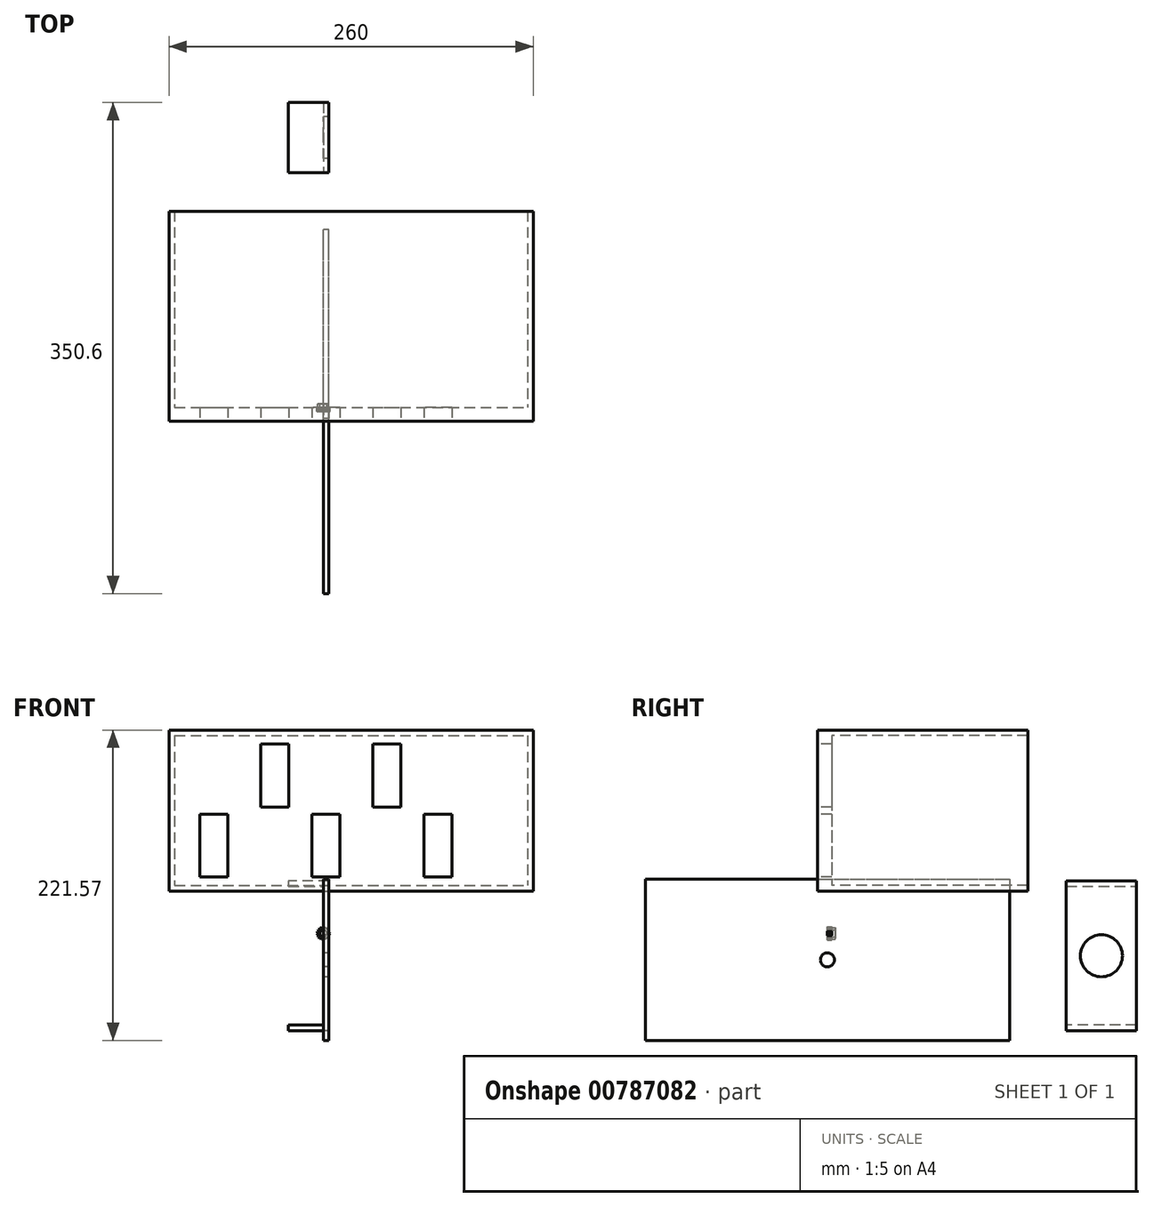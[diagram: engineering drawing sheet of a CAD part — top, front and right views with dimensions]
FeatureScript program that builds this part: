
annotation { "Feature Type Name" : "Feature", "Feature Type Description" : "" }
export const myFeature = defineFeature(function(context is Context, id is Id, definition is map)
    precondition{}
    {
        {
            var Q0;
            Q0=qCreatedBy(makeId("Front.planeOp"),FACE);
            var sketch = newSketch(context, id + "F0", { "sketchPlane" : qUnion([Q0])});
            skCircle(sketch, "E0", {"center": v(0, 0) * mm, "radius": 4 * mm});
            skCircle(sketch, "E1", {"center": v(0, 0) * mm, "radius": 2.5 * mm});
            skLineSegment(sketch, "E2", {"start": v(-2.75, 2.9) * mm, "end": v(-2.68, 3.9) * mm});
            skLineSegment(sketch, "E3", {"start": v(-2.68, 3.9) * mm, "end": v(-1.73, 3.6) * mm});
            skLineSegment(sketch, "E4.1.0", {"start": v(-3.51, 1.9) * mm, "end": v(-3.76, 2.88) * mm});
            skLineSegment(sketch, "E4.1.1", {"start": v(-3.76, 2.88) * mm, "end": v(-2.76, 2.9) * mm});
            skLineSegment(sketch, "E4.2.0", {"start": v(-3.93, 0.73) * mm, "end": v(-4.46, 1.58) * mm});
            skLineSegment(sketch, "E4.2.1", {"start": v(-4.46, 1.58) * mm, "end": v(-3.52, 1.9) * mm});
            skLineSegment(sketch, "E4.3.0", {"start": v(-3.96, -0.52) * mm, "end": v(-4.73, 0.12) * mm});
            skLineSegment(sketch, "E4.3.1", {"start": v(-4.73, 0.12) * mm, "end": v(-3.93, 0.72) * mm});
            skLineSegment(sketch, "E4.4.0", {"start": v(-3.6, -1.72) * mm, "end": v(-4.54, -1.35) * mm});
            skLineSegment(sketch, "E4.4.1", {"start": v(-4.54, -1.35) * mm, "end": v(-3.96, -0.53) * mm});
            skLineSegment(sketch, "E4.5.0", {"start": v(-2.9, -2.75) * mm, "end": v(-3.9, -2.68) * mm});
            skLineSegment(sketch, "E4.5.1", {"start": v(-3.9, -2.68) * mm, "end": v(-3.6, -1.73) * mm});
            skLineSegment(sketch, "E4.6.0", {"start": v(-1.9, -3.51) * mm, "end": v(-2.88, -3.76) * mm});
            skLineSegment(sketch, "E4.6.1", {"start": v(-2.88, -3.76) * mm, "end": v(-2.9, -2.76) * mm});
            skLineSegment(sketch, "E4.7.0", {"start": v(-0.73, -3.93) * mm, "end": v(-1.58, -4.46) * mm});
            skLineSegment(sketch, "E4.7.1", {"start": v(-1.58, -4.46) * mm, "end": v(-1.9, -3.52) * mm});
            skLineSegment(sketch, "E4.8.0", {"start": v(0.52, -3.96) * mm, "end": v(-0.12, -4.73) * mm});
            skLineSegment(sketch, "E4.8.1", {"start": v(-0.12, -4.73) * mm, "end": v(-0.72, -3.93) * mm});
            skLineSegment(sketch, "E4.9.0", {"start": v(1.72, -3.6) * mm, "end": v(1.35, -4.54) * mm});
            skLineSegment(sketch, "E4.9.1", {"start": v(1.35, -4.54) * mm, "end": v(0.53, -3.96) * mm});
            skLineSegment(sketch, "E5.1.10.0", {"start": v(2.75, -2.9) * mm, "end": v(2.68, -3.9) * mm});
            skLineSegment(sketch, "E5.3.10.0", {"start": v(2.68, -3.9) * mm, "end": v(1.73, -3.6) * mm});
            skLineSegment(sketch, "E6.1.11.0", {"start": v(3.51, -1.9) * mm, "end": v(3.76, -2.88) * mm});
            skLineSegment(sketch, "E6.3.11.0", {"start": v(3.76, -2.88) * mm, "end": v(2.76, -2.9) * mm});
            skLineSegment(sketch, "E6.1.12.0", {"start": v(3.93, -0.73) * mm, "end": v(4.46, -1.58) * mm});
            skLineSegment(sketch, "E6.3.12.0", {"start": v(4.46, -1.58) * mm, "end": v(3.52, -1.9) * mm});
            skLineSegment(sketch, "E6.1.13.0", {"start": v(3.96, 0.52) * mm, "end": v(4.73, -0.12) * mm});
            skLineSegment(sketch, "E6.3.13.0", {"start": v(4.73, -0.12) * mm, "end": v(3.93, -0.72) * mm});
            skLineSegment(sketch, "E6.1.14.0", {"start": v(3.6, 1.72) * mm, "end": v(4.54, 1.35) * mm});
            skLineSegment(sketch, "E6.3.14.0", {"start": v(4.54, 1.35) * mm, "end": v(3.96, 0.53) * mm});
            skLineSegment(sketch, "E7.1.15.0", {"start": v(2.9, 2.75) * mm, "end": v(3.9, 2.68) * mm});
            skLineSegment(sketch, "E7.3.15.0", {"start": v(3.9, 2.68) * mm, "end": v(3.6, 1.73) * mm});
            skLineSegment(sketch, "E8.1.16.0", {"start": v(1.9, 3.51) * mm, "end": v(2.88, 3.76) * mm});
            skLineSegment(sketch, "E8.3.16.0", {"start": v(2.88, 3.76) * mm, "end": v(2.9, 2.76) * mm});
            skLineSegment(sketch, "E9.1.17.0", {"start": v(0.73, 3.93) * mm, "end": v(1.58, 4.46) * mm});
            skLineSegment(sketch, "E9.3.17.0", {"start": v(1.58, 4.46) * mm, "end": v(1.9, 3.52) * mm});
            skLineSegment(sketch, "E10.1.18.0", {"start": v(-0.52, 3.96) * mm, "end": v(0.12, 4.73) * mm});
            skLineSegment(sketch, "E10.3.18.0", {"start": v(0.12, 4.73) * mm, "end": v(0.72, 3.93) * mm});
            skLineSegment(sketch, "E11.1.19.0", {"start": v(-1.72, 3.6) * mm, "end": v(-1.35, 4.54) * mm});
            skLineSegment(sketch, "E11.3.19.0", {"start": v(-1.35, 4.54) * mm, "end": v(-0.53, 3.96) * mm});
            skSolve(sketch);
        }
        {
            var Q0;
            Q0 = qSketchRegion(id + "F0", true);
            extrude(context, id + "F1", {"entities" : qUnion([Q0]), "depth" : 3 * mm, "offsetDistance" : 25 * mm});
        }
        {
            var Q0;
            Q0=makeQuery(id+"F0.imprint","IMPRINT",FACE,{"disambiguationData":[TD([[makeQuery(id+"F0.imprint","IMPRINT",EDGE,{"derivedFrom":sQuery(id+"F0.wireOp",EDGE,"E1")}),-1.0]])]});
            extrude(context, id + "F2", {"entities" : qUnion([Q0]), "operationType" : NewBodyOperationType.ADD, "oppositeDirection" : true, "depth" : 2.5 * mm, "offsetDistance" : 25 * mm});
        }
        {
            var Q0;
            Q0=qCreatedBy(makeId("Front.planeOp"),FACE);
            var sketch = newSketch(context, id + "F3", { "sketchPlane" : qUnion([Q0])});
            skLineSegment(sketch, "E12.bottom", {"start": v(-110.14, 145.15) * mm, "end": v(149.86, 145.15) * mm});
            skLineSegment(sketch, "E12.top", {"start": v(-110.14, 30.15) * mm, "end": v(149.86, 30.15) * mm});
            skLineSegment(sketch, "E12.left", {"start": v(-110.14, 145.15) * mm, "end": v(-110.14, 30.15) * mm});
            skLineSegment(sketch, "E12.right", {"start": v(149.86, 145.15) * mm, "end": v(149.86, 30.15) * mm});
            skSolve(sketch);
        }
        {
            var Q0;
            Q0=makeQuery(id+"F3.imprint","IMPRINT",FACE,{"disambiguationData":[TD([[makeQuery(id+"F3.imprint","IMPRINT",EDGE,{"derivedFrom":sQuery(id+"F3.wireOp",EDGE,"E12.bottom")}),-1.0]])]});
            extrude(context, id + "F4", {"entities" : qUnion([Q0]), "depth" : 10 * mm, "offsetDistance" : 25 * mm});
        }
        {
            var Q0;
            Q0=makeQuery(id+"F4.opExtrude","CAP_FACE",FACE,{"disambiguationData":[OSD([sQuery(id+"F3.wireOp",EDGE,"E12.bottom"),sQuery(id+"F3.wireOp",EDGE,"E12.top"),sQuery(id+"F3.wireOp",EDGE,"E12.left"),sQuery(id+"F3.wireOp",EDGE,"E12.right")])],"isStart":false});
            var sketch = newSketch(context, id + "F5", { "sketchPlane" : qUnion([Q0])});
            skLineSegment(sketch, "E13.bottom", {"start": v(-88.14, 85.15) * mm, "end": v(-68.14, 85.15) * mm});
            skLineSegment(sketch, "E13.top", {"start": v(-88.14, 40.15) * mm, "end": v(-68.14, 40.15) * mm});
            skLineSegment(sketch, "E13.left", {"start": v(-88.14, 85.15) * mm, "end": v(-88.14, 40.15) * mm});
            skLineSegment(sketch, "E13.right", {"start": v(-68.14, 85.15) * mm, "end": v(-68.14, 40.15) * mm});
            skLineSegment(sketch, "E14", {"start": v(-88.14, 40.15) * mm, "end": v(99, 40.15) * mm, "construction": true});
            skLineSegment(sketch, "E15.bottom", {"start": v(11.86, 40.15) * mm, "end": v(-8.14, 40.15) * mm});
            skLineSegment(sketch, "E15.top", {"start": v(11.86, 85.15) * mm, "end": v(-8.14, 85.15) * mm});
            skLineSegment(sketch, "E15.left", {"start": v(11.86, 40.15) * mm, "end": v(11.86, 85.15) * mm});
            skLineSegment(sketch, "E15.right", {"start": v(-8.14, 40.15) * mm, "end": v(-8.14, 85.15) * mm});
            skLineSegment(sketch, "E16.bottom", {"start": v(91.86, 40.15) * mm, "end": v(71.86, 40.15) * mm});
            skLineSegment(sketch, "E16.top", {"start": v(91.86, 85.15) * mm, "end": v(71.86, 85.15) * mm});
            skLineSegment(sketch, "E16.left", {"start": v(71.86, 40.15) * mm, "end": v(71.86, 85.15) * mm});
            skLineSegment(sketch, "E16.right", {"start": v(91.86, 40.15) * mm, "end": v(91.86, 85.15) * mm});
            skLineSegment(sketch, "E17", {"start": v(-110.14, 135.15) * mm, "end": v(149.86, 135.15) * mm, "construction": true});
            skLineSegment(sketch, "E18.bottom", {"start": v(-44.77, 135.15) * mm, "end": v(-24.77, 135.15) * mm});
            skLineSegment(sketch, "E18.top", {"start": v(-44.77, 90.15) * mm, "end": v(-24.77, 90.15) * mm});
            skLineSegment(sketch, "E18.left", {"start": v(-44.77, 135.15) * mm, "end": v(-44.77, 90.15) * mm});
            skLineSegment(sketch, "E18.right", {"start": v(-24.77, 135.15) * mm, "end": v(-24.77, 90.15) * mm});
            skLineSegment(sketch, "E19.bottom", {"start": v(35.23, 135.15) * mm, "end": v(55.23, 135.15) * mm});
            skLineSegment(sketch, "E19.top", {"start": v(35.23, 90.15) * mm, "end": v(55.23, 90.15) * mm});
            skLineSegment(sketch, "E19.left", {"start": v(35.23, 135.15) * mm, "end": v(35.23, 90.15) * mm});
            skLineSegment(sketch, "E19.right", {"start": v(55.23, 135.15) * mm, "end": v(55.23, 90.15) * mm});
            skSolve(sketch);
        }
        {
            var Q0;
            Q0=makeQuery(id+"F5.imprint","IMPRINT",FACE,{"disambiguationData":[TD([[makeQuery(id+"F5.imprint","IMPRINT",EDGE,{"derivedFrom":sQuery(id+"F5.wireOp",EDGE,"E13.bottom")}),-1.0]])]});
            var Q1;
            Q1=makeQuery(id+"F5.imprint","IMPRINT",FACE,{"disambiguationData":[TD([[makeQuery(id+"F5.imprint","IMPRINT",EDGE,{"derivedFrom":sQuery(id+"F5.wireOp",EDGE,"E15.bottom")}),-1.0]])]});
            var Q2;
            Q2=makeQuery(id+"F5.imprint","IMPRINT",FACE,{"disambiguationData":[TD([[makeQuery(id+"F5.imprint","IMPRINT",EDGE,{"derivedFrom":sQuery(id+"F5.wireOp",EDGE,"E16.bottom")}),-1.0]])]});
            var Q3;
            Q3=makeQuery(id+"F5.imprint","IMPRINT",FACE,{"disambiguationData":[TD([[makeQuery(id+"F5.imprint","IMPRINT",EDGE,{"derivedFrom":sQuery(id+"F5.wireOp",EDGE,"E19.bottom")}),-1.0]])]});
            var Q4;
            Q4=makeQuery(id+"F5.imprint","IMPRINT",FACE,{"disambiguationData":[TD([[makeQuery(id+"F5.imprint","IMPRINT",EDGE,{"derivedFrom":sQuery(id+"F5.wireOp",EDGE,"E18.bottom")}),-1.0]])]});
            extrude(context, id + "F6", {"entities" : qUnion([Q0, Q1, Q2, Q3, Q4]), "operationType" : NewBodyOperationType.REMOVE, "endBound" : BoundingType.THROUGH_ALL, "oppositeDirection" : true, "depth" : 25 * mm, "offsetDistance" : 25 * mm});
        }
        {
            var Q0;
            Q0=makeQuery(id+"F4.opExtrude","CAP_FACE",FACE,{"disambiguationData":[OSD([sQuery(id+"F3.wireOp",EDGE,"E12.bottom"),sQuery(id+"F3.wireOp",EDGE,"E12.top"),sQuery(id+"F3.wireOp",EDGE,"E12.left"),sQuery(id+"F3.wireOp",EDGE,"E12.right")])],"isStart":false});
            var sketch = newSketch(context, id + "F7", { "sketchPlane" : qUnion([Q0])});
            skLineSegment(sketch, "E20.bottom", {"start": v(-106.14, 141.15) * mm, "end": v(145.86, 141.15) * mm});
            skLineSegment(sketch, "E20.top", {"start": v(-106.14, 34.15) * mm, "end": v(145.86, 34.15) * mm});
            skLineSegment(sketch, "E20.left", {"start": v(-106.14, 141.15) * mm, "end": v(-106.14, 34.15) * mm});
            skLineSegment(sketch, "E20.right", {"start": v(145.86, 141.15) * mm, "end": v(145.86, 34.15) * mm});
            skSolve(sketch);
        }
        {
            var Q0;
            Q0=makeQuery(id+"F7.imprint","IMPRINT",FACE,{"disambiguationData":[TD([[makeQuery(id+"F7.imprint","IMPRINT",EDGE,{"derivedFrom":sQuery(id+"F7.wireOp",EDGE,"E20.bottom")}),1.0]])]});
            extrude(context, id + "F8", {"entities" : qUnion([Q0]), "operationType" : NewBodyOperationType.ADD, "oppositeDirection" : true, "depth" : 150 * mm, "offsetDistance" : 25 * mm});
        }
        {
            var Q0;
            Q0=qCreatedBy(makeId("Right.planeOp"),FACE);
            var sketch = newSketch(context, id + "F9", { "sketchPlane" : qUnion([Q0])});
            skLineSegment(sketch, "E21.bottom", {"start": v(-133.08, 38.58) * mm, "end": v(126.92, 38.58) * mm});
            skLineSegment(sketch, "E21.top", {"start": v(-133.08, -76.42) * mm, "end": v(126.92, -76.42) * mm});
            skLineSegment(sketch, "E21.left", {"start": v(-133.08, 38.58) * mm, "end": v(-133.08, -76.42) * mm});
            skLineSegment(sketch, "E21.right", {"start": v(126.92, 38.58) * mm, "end": v(126.92, -76.42) * mm});
            skSolve(sketch);
        }
        {
            var Q0;
            Q0 = qSketchRegion(id + "F9", true);
            extrude(context, id + "F10", {"entities" : qUnion([Q0]), "depth" : 4 * mm, "offsetDistance" : 25 * mm});
        }
        {
            var Q0;
            Q0=makeQuery(id+"F10.opExtrude","CAP_FACE",FACE,{"disambiguationData":[OSD([sQuery(id+"F9.wireOp",EDGE,"E21.bottom"),sQuery(id+"F9.wireOp",EDGE,"E21.top"),sQuery(id+"F9.wireOp",EDGE,"E21.left"),sQuery(id+"F9.wireOp",EDGE,"E21.right")])],"isStart":true});
            var sketch = newSketch(context, id + "F11", { "sketchPlane" : qUnion([Q0])});
            skPoint(sketch, "E22", {"position": v(3.08, -18.92) * mm});
            skSolve(sketch);
        }
        {
            var Q0;
            Q0=sQuery(id+"F11.wireOp",VERTEX,"E22");
            var Q1;
            Q1=makeQuery(id+"F10.opExtrude","SWEPT_BODY",BODY,{"disambiguationData":[OSD([sQuery(id+"F9.wireOp",EDGE,"E21.bottom"),sQuery(id+"F9.wireOp",EDGE,"E21.top"),sQuery(id+"F9.wireOp",EDGE,"E21.left"),sQuery(id+"F9.wireOp",EDGE,"E21.right")])]});
            hole(context, id + "F12", {"style" : HoleStyle.SIMPLE, "endStyle" : HoleEndStyle.THROUGH, "holeDiameter" : 10 * mm, "majorDiameter" : 5 * mm, "isTappedThrough" : true, "tappedDepth" : 12 * mm, "tapClearance" : 3, "startFromSketch" : true, "locations" : qUnion([Q0]), "scope" : qUnion([Q1])});
        }
        {
            var Q0;
            Q0=qCreatedBy(makeId("Right.planeOp"),FACE);
            var sketch = newSketch(context, id + "F13", { "sketchPlane" : qUnion([Q0])});
            skLineSegment(sketch, "E23.bottom", {"start": v(217.52, 37.5) * mm, "end": v(167.52, 37.5) * mm});
            skLineSegment(sketch, "E23.top", {"start": v(217.52, -69.5) * mm, "end": v(167.52, -69.5) * mm});
            skLineSegment(sketch, "E23.left", {"start": v(217.52, 37.5) * mm, "end": v(217.52, -69.5) * mm});
            skLineSegment(sketch, "E23.right", {"start": v(167.52, 37.5) * mm, "end": v(167.52, -69.5) * mm});
            skLineSegment(sketch, "E24.left", {"start": v(217.52, 37.5) * mm, "end": v(217.52, 33.5) * mm});
            skLineSegment(sketch, "E24.right", {"start": v(167.52, 37.5) * mm, "end": v(167.52, 33.5) * mm});
            skLineSegment(sketch, "E25.bottom", {"start": v(167.52, -69.5) * mm, "end": v(217.52, -69.5) * mm});
            skLineSegment(sketch, "E25.left", {"start": v(167.52, -69.5) * mm, "end": v(167.52, -65.5) * mm});
            skLineSegment(sketch, "E25.right", {"start": v(217.52, -69.5) * mm, "end": v(217.52, -65.5) * mm});
            skPoint(sketch, "E26", {"position": v(192.52, -16) * mm});
            skSolve(sketch);
        }
        {
            var Q0;
            Q0 = qSketchRegion(id + "F13", true);
            extrude(context, id + "F14", {"entities" : qUnion([Q0]), "depth" : 4 * mm, "offsetDistance" : 25 * mm});
        }
        {
            var Q0;
            Q0=makeQuery(id+"F14.opExtrude","CAP_FACE",FACE,{"disambiguationData":[OSD([sQuery(id+"F13.wireOp",EDGE,"E23.left"),sQuery(id+"F13.wireOp",EDGE,"E23.right"),sQuery(id+"F13.wireOp",EDGE,"E23.bottom"),sQuery(id+"F13.wireOp",EDGE,"E24.left"),sQuery(id+"F13.wireOp",EDGE,"E24.right"),sQuery(id+"F13.wireOp",EDGE,"E25.bottom"),sQuery(id+"F13.wireOp",EDGE,"E25.left"),sQuery(id+"F13.wireOp",EDGE,"E25.right")])],"isStart":true});
            var sketch = newSketch(context, id + "F15", { "sketchPlane" : qUnion([Q0])});
            skLineSegment(sketch, "E27.bottom", {"start": v(-167.52, 37.5) * mm, "end": v(-217.52, 37.5) * mm});
            skLineSegment(sketch, "E27.top", {"start": v(-167.52, 33.5) * mm, "end": v(-217.52, 33.5) * mm});
            skLineSegment(sketch, "E27.left", {"start": v(-167.52, 37.5) * mm, "end": v(-167.52, 33.5) * mm});
            skLineSegment(sketch, "E27.right", {"start": v(-217.52, 37.5) * mm, "end": v(-217.52, 33.5) * mm});
            skLineSegment(sketch, "E28.bottom", {"start": v(-217.52, -69.5) * mm, "end": v(-167.52, -69.5) * mm});
            skLineSegment(sketch, "E28.top", {"start": v(-217.52, -65.5) * mm, "end": v(-167.52, -65.5) * mm});
            skLineSegment(sketch, "E28.left", {"start": v(-217.52, -69.5) * mm, "end": v(-217.52, -65.5) * mm});
            skLineSegment(sketch, "E28.right", {"start": v(-167.52, -69.5) * mm, "end": v(-167.52, -65.5) * mm});
            skSolve(sketch);
        }
        {
            var Q0;
            Q0 = qSketchRegion(id + "F15", true);
            extrude(context, id + "F16", {"entities" : qUnion([Q0]), "operationType" : NewBodyOperationType.ADD, "depth" : 25 * mm, "offsetDistance" : 25 * mm});
        }
        {
            var Q0;
            Q0=sQuery(id+"F13.wireOp",VERTEX,"E26");
            var Q1;
            Q1=makeQuery(id+"F14.opExtrude","SWEPT_BODY",BODY,{"disambiguationData":[OSD([sQuery(id+"F13.wireOp",EDGE,"E23.left"),sQuery(id+"F13.wireOp",EDGE,"E23.right"),sQuery(id+"F13.wireOp",EDGE,"E23.bottom"),sQuery(id+"F13.wireOp",EDGE,"E24.left"),sQuery(id+"F13.wireOp",EDGE,"E24.right"),sQuery(id+"F13.wireOp",EDGE,"E25.bottom"),sQuery(id+"F13.wireOp",EDGE,"E25.left"),sQuery(id+"F13.wireOp",EDGE,"E25.right")])]});
            hole(context, id + "F17", {"style" : HoleStyle.SIMPLE, "endStyle" : HoleEndStyle.THROUGH, "oppositeDirection" : true, "holeDiameter" : 30 * mm, "majorDiameter" : 5 * mm, "isTappedThrough" : true, "tappedDepth" : 12 * mm, "tapClearance" : 3, "startFromSketch" : true, "locations" : qUnion([Q0]), "scope" : qUnion([Q1])});
        }
    });
